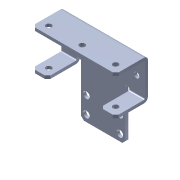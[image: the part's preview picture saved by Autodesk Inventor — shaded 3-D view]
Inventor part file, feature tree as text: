
AUTODESK INVENTOR PART (.ipt)
format: ipt  version: 2013 (Build 170138000, 138)  size: 136,192 bytes
history: native  units: in
note: dims shown in document units (in); Inventor stores cm internally (conversion verified against a paired STEP export)
features: chamfer x1, other x1, imported_body x1
ambient origin geometry x8: Origin, YZ Plane, XZ Plane, XY Plane, X Axis, Y Axis, Z Axis, Center Point
feature tree (3):
  chamfer  "Chamfer1"  [1 undecoded]
  other  "217-3558-STEP1"
  imported_body  "Base1"
note: 1 required parameter value undecoded (feature->parameter linkage not recoverable at this tier; creation-order binding heuristic only, values carry confidence <= 0.55)
